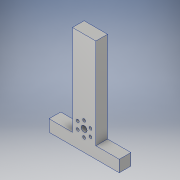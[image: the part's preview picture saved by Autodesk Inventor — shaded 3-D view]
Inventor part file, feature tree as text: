
AUTODESK INVENTOR PART (.ipt)
format: ipt  version: 2019 (Build 230136000, 136)  size: 139,264 bytes
history: native  units: in
note: dims shown in document units (in); Inventor stores cm internally (conversion verified against a paired STEP export)
features: sketch x4, extrude x2, hole x2, pattern_circular x1, plane x1, mirror x1
ambient origin geometry x8: Origin, YZ Plane, XZ Plane, XY Plane, X Axis, Y Axis, Z Axis, Center Point
bodies: Solid1 (feature_tree)
feature tree (11):
  extrude  "Extrusion1"  Depth=4.375in
  hole  "Hole1"  [1 undecoded]
  hole  "Hole2"  [1 undecoded]
  pattern_circular  "Circular Pattern1"  [2 undecoded]
  extrude  "Extrusion2"  Depth=0.5in
  plane  "Work Plane1"
  mirror  "Mirror1"
  sketch  "Sketch1"  dims[d0=1.0in d1=4.375in]
  sketch  "Sketch2"  dims[d2=0.5in d3=0.0in d4=3.5in]
  sketch  "Sketch3"  dims[d5=1.0in d6=0.5in]
  sketch  "Sketch5"  dims[d7=0.25in d8=0.75in d9=0.375in d10=0.25in d11=0.5635in d12=1.0in d13=0.8108in d14=0.315in d15=0.5in d16=0.125in d17=0.75in d18=0.375in d19=0.25in d20=0.5635in d21=1.0in d22=0.8108in d23=2.3622in d24=360.0deg d26=0.5in d27=1.0in d28=0.0in]
note: 4 required parameter values undecoded (feature->parameter linkage not recoverable at this tier; creation-order binding heuristic only, values carry confidence <= 0.55)
